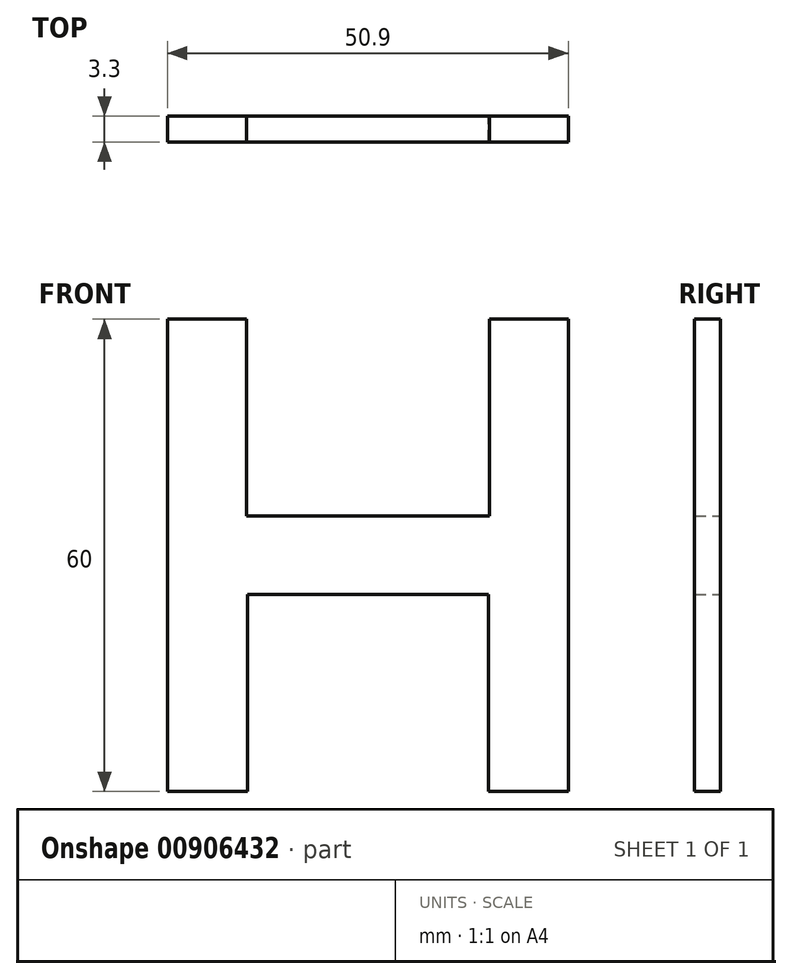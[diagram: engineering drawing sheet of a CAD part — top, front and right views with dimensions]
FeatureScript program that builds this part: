
annotation { "Feature Type Name" : "Feature", "Feature Type Description" : "" }
export const myFeature = defineFeature(function(context is Context, id is Id, definition is map)
    precondition{}
    {
        {
            var Q0;
            Q0=qCreatedBy(makeId("Front.planeOp"),FACE);
            var sketch = newSketch(context, id + "F0", { "sketchPlane" : qUnion([Q0])});
            skLineSegment(sketch, "E0", {"start": v(0, 0.94) * mm, "end": v(15.45, 0.94) * mm});
            skLineSegment(sketch, "E1", {"start": v(15.45, 0.94) * mm, "end": v(15.45, 25.94) * mm});
            skLineSegment(sketch, "E2", {"start": v(15.45, 25.94) * mm, "end": v(25.45, 25.94) * mm});
            skLineSegment(sketch, "E3", {"start": v(25.45, 25.94) * mm, "end": v(25.45, -34.06) * mm});
            skLineSegment(sketch, "E4", {"start": v(25.45, -34.06) * mm, "end": v(15.3, -34.06) * mm});
            skLineSegment(sketch, "E5", {"start": v(15.3, -34.06) * mm, "end": v(15.3, -9.06) * mm});
            skLineSegment(sketch, "E6", {"start": v(15.3, -9.06) * mm, "end": v(0, -9.06) * mm});
            skLineSegment(sketch, "E7.MirrorCS", {"start": v(-15.45, 25.94) * mm, "end": v(-25.45, 25.94) * mm});
            skLineSegment(sketch, "E8.MirrorCS", {"start": v(-25.45, 25.94) * mm, "end": v(-25.45, -34.06) * mm});
            skLineSegment(sketch, "E9.MirrorCS", {"start": v(-15.3, -34.06) * mm, "end": v(-15.3, -9.06) * mm});
            skLineSegment(sketch, "E10.MirrorCS", {"start": v(-25.45, -34.06) * mm, "end": v(-15.3, -34.06) * mm});
            skLineSegment(sketch, "E11.MirrorCS", {"start": v(-15.45, 0.94) * mm, "end": v(-15.45, 25.94) * mm});
            skLineSegment(sketch, "E12.MirrorCS", {"start": v(0, 0.94) * mm, "end": v(-15.45, 0.94) * mm});
            skLineSegment(sketch, "E13.MirrorCS", {"start": v(-15.3, -9.06) * mm, "end": v(0, -9.06) * mm});
            skSolve(sketch);
        }
        {
            var Q0;
            Q0=makeQuery(id+"F0.imprint","IMPRINT",FACE,{"disambiguationData":[TD([[makeQuery(id+"F0.imprint","IMPRINT",EDGE,{"derivedFrom":sQuery(id+"F0.wireOp",EDGE,"E0")}),-1.0]])]});
            extrude(context, id + "F1", {"entities" : qUnion([Q0]), "depth" : 3.3 * mm, "offsetDistance" : 25 * mm});
        }
    });
